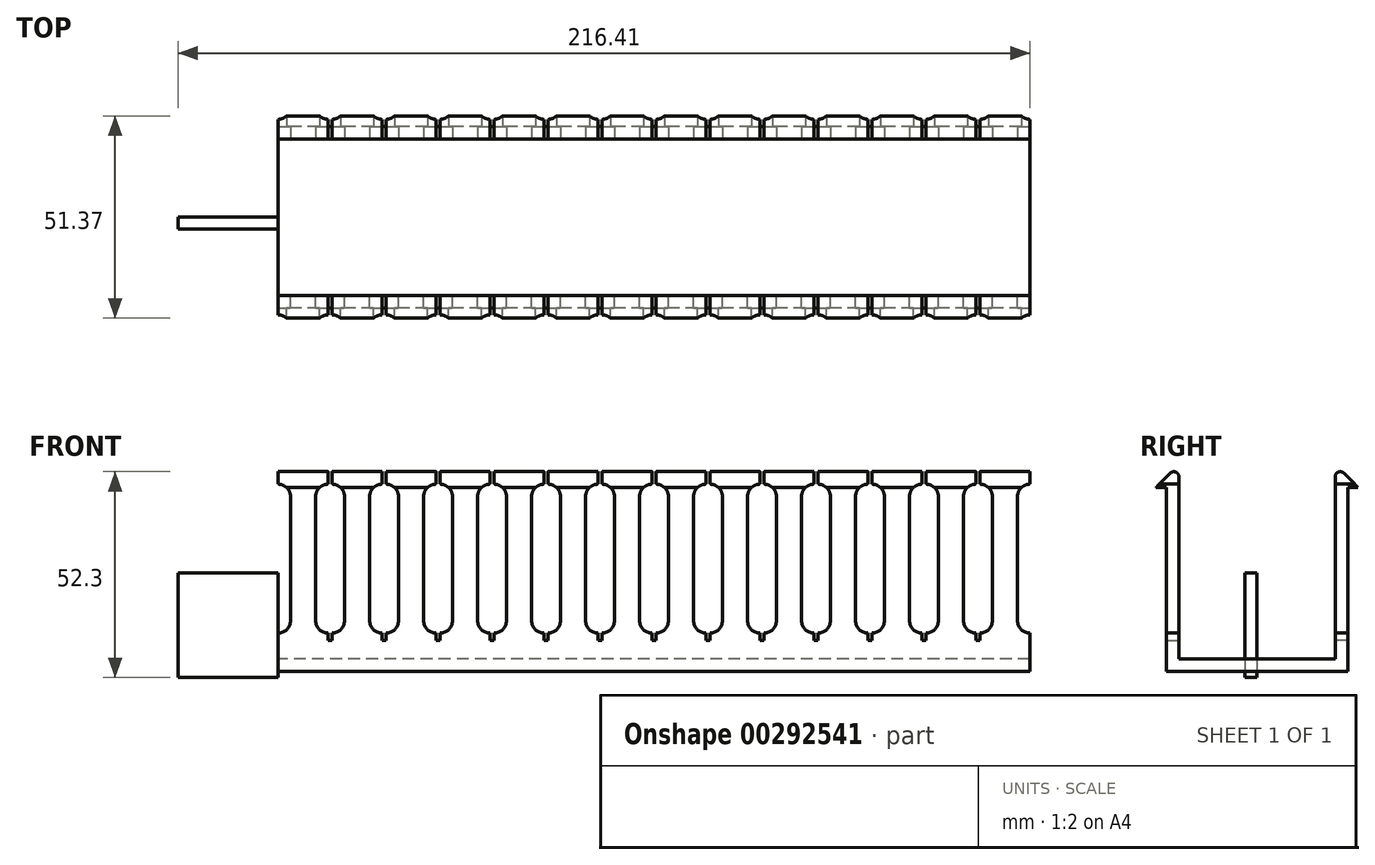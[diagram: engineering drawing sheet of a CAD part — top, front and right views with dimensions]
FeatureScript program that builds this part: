
annotation { "Feature Type Name" : "Feature", "Feature Type Description" : "" }
export const myFeature = defineFeature(function(context is Context, id is Id, definition is map)
    precondition{}
    {
        {
            var Q0;
            Q0=qCreatedBy(makeId("Front.planeOp"),FACE);
            var sketch = newSketch(context, id + "F0", { "sketchPlane" : qUnion([Q0])});
            skLineSegment(sketch, "E0", {"start": v(0, 47.62) * mm, "end": v(0, 50.8) * mm});
            skLineSegment(sketch, "E1", {"start": v(0, 50.8) * mm, "end": v(12.7, 50.8) * mm});
            skLineSegment(sketch, "E2", {"start": v(12.7, 50.8) * mm, "end": v(12.7, 47.62) * mm});
            skArc(sketch, "E3", {"start": v(3.18, 44.45) * mm, "mid": v(2.25, 46.7) * mm, "end": v(0, 47.62) * mm});
            skArc(sketch, "E4", {"start": v(12.7, 47.62) * mm, "mid": v(10.45, 46.7) * mm, "end": v(9.53, 44.45) * mm});
            skLineSegment(sketch, "E5", {"start": v(3.18, 44.45) * mm, "end": v(3.18, 12.95) * mm});
            skLineSegment(sketch, "E6", {"start": v(9.53, 44.45) * mm, "end": v(9.53, 12.95) * mm});
            skArc(sketch, "E7", {"start": v(3.18, 12.95) * mm, "mid": v(2.25, 10.7) * mm, "end": v(0, 9.78) * mm});
            skArc(sketch, "E8", {"start": v(9.53, 12.95) * mm, "mid": v(10.45, 10.7) * mm, "end": v(12.7, 9.78) * mm});
            skLineSegment(sketch, "E9", {"start": v(0, 9.78) * mm, "end": v(0, 0) * mm});
            skLineSegment(sketch, "E10", {"start": v(0, 0) * mm, "end": v(191, 0) * mm});
            skLineSegment(sketch, "E11", {"start": v(13.2, 7.13) * mm, "end": v(13.2, 52.31) * mm, "construction": true});
            skLineSegment(sketch, "E12.MirrorCS", {"start": v(13.72, 50.8) * mm, "end": v(13.72, 47.62) * mm});
            skArc(sketch, "E13.MirrorCS", {"start": v(13.72, 47.62) * mm, "mid": v(15.96, 46.7) * mm, "end": v(16.9, 44.45) * mm});
            skLineSegment(sketch, "E14.MirrorCS", {"start": v(16.9, 44.45) * mm, "end": v(16.9, 12.95) * mm});
            skArc(sketch, "E15.MirrorCS", {"start": v(16.9, 12.95) * mm, "mid": v(15.96, 10.7) * mm, "end": v(13.72, 9.78) * mm});
            skLineSegment(sketch, "E16.MirrorCS", {"start": v(26.42, 50.8) * mm, "end": v(13.72, 50.8) * mm});
            skLineSegment(sketch, "E17.MirrorCS", {"start": v(26.42, 47.62) * mm, "end": v(26.42, 50.8) * mm});
            skArc(sketch, "E18.MirrorCS", {"start": v(23.24, 44.45) * mm, "mid": v(24.17, 46.7) * mm, "end": v(26.42, 47.62) * mm});
            skLineSegment(sketch, "E19.MirrorCS", {"start": v(23.24, 44.45) * mm, "end": v(23.24, 12.95) * mm});
            skArc(sketch, "E20.MirrorCS", {"start": v(23.24, 12.95) * mm, "mid": v(24.17, 10.7) * mm, "end": v(26.42, 9.78) * mm});
            skLineSegment(sketch, "E21", {"start": v(26.92, 7.21) * mm, "end": v(26.92, 55.4) * mm, "construction": true});
            skLineSegment(sketch, "E22.MirrorCS", {"start": v(27.43, 47.62) * mm, "end": v(27.43, 50.8) * mm});
            skArc(sketch, "E23.MirrorCS", {"start": v(30.6, 44.45) * mm, "mid": v(29.68, 46.7) * mm, "end": v(27.43, 47.62) * mm});
            skLineSegment(sketch, "E24.MirrorCS", {"start": v(30.6, 44.45) * mm, "end": v(30.6, 12.95) * mm});
            skArc(sketch, "E25.MirrorCS", {"start": v(30.6, 12.95) * mm, "mid": v(29.68, 10.7) * mm, "end": v(27.43, 9.78) * mm});
            skLineSegment(sketch, "E26.MirrorCS", {"start": v(27.43, 50.8) * mm, "end": v(40.13, 50.8) * mm});
            skLineSegment(sketch, "E27.MirrorCS", {"start": v(40.13, 50.8) * mm, "end": v(40.13, 47.62) * mm});
            skArc(sketch, "E28.MirrorCS", {"start": v(40.13, 47.62) * mm, "mid": v(37.89, 46.7) * mm, "end": v(36.96, 44.45) * mm});
            skLineSegment(sketch, "E29.MirrorCS", {"start": v(36.96, 44.45) * mm, "end": v(36.96, 12.95) * mm});
            skArc(sketch, "E30.MirrorCS", {"start": v(36.96, 12.95) * mm, "mid": v(37.89, 10.7) * mm, "end": v(40.13, 9.78) * mm});
            skLineSegment(sketch, "E31", {"start": v(40.64, 6.35) * mm, "end": v(40.64, 55.95) * mm, "construction": true});
            skLineSegment(sketch, "E32.MirrorCS", {"start": v(41.15, 50.8) * mm, "end": v(41.15, 47.62) * mm});
            skLineSegment(sketch, "E33.MirrorCS", {"start": v(53.85, 50.8) * mm, "end": v(41.15, 50.8) * mm});
            skArc(sketch, "E34.MirrorCS", {"start": v(41.15, 47.62) * mm, "mid": v(43.4, 46.7) * mm, "end": v(44.32, 44.45) * mm});
            skArc(sketch, "E35.MirrorCS", {"start": v(50.67, 44.45) * mm, "mid": v(51.6, 46.7) * mm, "end": v(53.85, 47.62) * mm});
            skLineSegment(sketch, "E36.MirrorCS", {"start": v(50.67, 44.45) * mm, "end": v(50.67, 12.95) * mm});
            skLineSegment(sketch, "E37.MirrorCS", {"start": v(44.32, 44.45) * mm, "end": v(44.32, 12.95) * mm});
            skArc(sketch, "E38.MirrorCS", {"start": v(50.67, 12.95) * mm, "mid": v(51.6, 10.7) * mm, "end": v(53.85, 9.78) * mm});
            skArc(sketch, "E39.MirrorCS", {"start": v(44.32, 12.95) * mm, "mid": v(43.4, 10.7) * mm, "end": v(41.15, 9.78) * mm});
            skLineSegment(sketch, "E40.MirrorCS", {"start": v(53.85, 47.62) * mm, "end": v(53.85, 50.8) * mm});
            skLineSegment(sketch, "E41.MirrorCS", {"start": v(54.86, 47.62) * mm, "end": v(54.86, 50.8) * mm});
            skLineSegment(sketch, "E42.MirrorCS", {"start": v(54.86, 50.8) * mm, "end": v(67.56, 50.8) * mm});
            skLineSegment(sketch, "E43.MirrorCS", {"start": v(58.04, 44.45) * mm, "end": v(58.04, 12.95) * mm});
            skArc(sketch, "E44.MirrorCS", {"start": v(58.04, 44.45) * mm, "mid": v(57.1, 46.7) * mm, "end": v(54.86, 47.62) * mm});
            skArc(sketch, "E45.MirrorCS", {"start": v(58.04, 12.95) * mm, "mid": v(57.1, 10.7) * mm, "end": v(54.86, 9.78) * mm});
            skLineSegment(sketch, "E46.MirrorCS", {"start": v(67.56, 50.8) * mm, "end": v(67.56, 47.62) * mm});
            skArc(sketch, "E47.MirrorCS", {"start": v(67.56, 47.62) * mm, "mid": v(65.32, 46.7) * mm, "end": v(64.39, 44.45) * mm});
            skLineSegment(sketch, "E48.MirrorCS", {"start": v(64.39, 44.45) * mm, "end": v(64.39, 12.95) * mm});
            skArc(sketch, "E49.MirrorCS", {"start": v(64.39, 12.95) * mm, "mid": v(65.32, 10.7) * mm, "end": v(67.56, 9.78) * mm});
            skArc(sketch, "E50.MirrorCS", {"start": v(68.58, 47.62) * mm, "mid": v(70.83, 46.7) * mm, "end": v(71.76, 44.45) * mm});
            skLineSegment(sketch, "E51.MirrorCS", {"start": v(68.58, 50.8) * mm, "end": v(68.58, 47.62) * mm});
            skLineSegment(sketch, "E52.MirrorCS", {"start": v(81.28, 50.8) * mm, "end": v(68.58, 50.8) * mm});
            skLineSegment(sketch, "E53.MirrorCS", {"start": v(81.28, 47.62) * mm, "end": v(81.28, 50.8) * mm});
            skArc(sketch, "E54.MirrorCS", {"start": v(78.1, 44.45) * mm, "mid": v(79.03, 46.7) * mm, "end": v(81.28, 47.62) * mm});
            skLineSegment(sketch, "E55.MirrorCS", {"start": v(78.1, 44.45) * mm, "end": v(78.1, 12.95) * mm});
            skLineSegment(sketch, "E56.MirrorCS", {"start": v(71.76, 44.45) * mm, "end": v(71.76, 12.95) * mm});
            skArc(sketch, "E57.MirrorCS", {"start": v(71.76, 12.95) * mm, "mid": v(70.83, 10.7) * mm, "end": v(68.58, 9.78) * mm});
            skArc(sketch, "E58.MirrorCS", {"start": v(78.1, 12.95) * mm, "mid": v(79.03, 10.7) * mm, "end": v(81.28, 9.78) * mm});
            skLineSegment(sketch, "E59", {"start": v(81.79, 5.79) * mm, "end": v(81.79, 59.1) * mm, "construction": true});
            skLineSegment(sketch, "E60.MirrorCS", {"start": v(109.73, 47.62) * mm, "end": v(109.73, 50.8) * mm});
            skLineSegment(sketch, "E61.MirrorCS", {"start": v(108.71, 47.62) * mm, "end": v(108.71, 50.8) * mm});
            skArc(sketch, "E62.MirrorCS", {"start": v(112.9, 44.45) * mm, "mid": v(111.97, 46.7) * mm, "end": v(109.73, 47.62) * mm});
            skLineSegment(sketch, "E63.MirrorCS", {"start": v(122.43, 50.8) * mm, "end": v(122.43, 47.62) * mm});
            skLineSegment(sketch, "E64.MirrorCS", {"start": v(123.44, 50.8) * mm, "end": v(123.44, 47.62) * mm});
            skArc(sketch, "E65.MirrorCS", {"start": v(96.01, 47.62) * mm, "mid": v(98.26, 46.7) * mm, "end": v(99.19, 44.45) * mm});
            skArc(sketch, "E66.MirrorCS", {"start": v(122.43, 47.62) * mm, "mid": v(120.18, 46.7) * mm, "end": v(119.25, 44.45) * mm});
            skLineSegment(sketch, "E67.MirrorCS", {"start": v(96.01, 50.8) * mm, "end": v(96.01, 47.62) * mm});
            skLineSegment(sketch, "E68.MirrorCS", {"start": v(95, 50.8) * mm, "end": v(95, 47.62) * mm});
            skLineSegment(sketch, "E69.MirrorCS", {"start": v(136.14, 47.62) * mm, "end": v(136.14, 50.8) * mm});
            skArc(sketch, "E70.MirrorCS", {"start": v(132.97, 12.95) * mm, "mid": v(133.9, 10.7) * mm, "end": v(136.14, 9.78) * mm});
            skArc(sketch, "E71.MirrorCS", {"start": v(149.86, 47.62) * mm, "mid": v(147.61, 46.7) * mm, "end": v(146.69, 44.45) * mm});
            skLineSegment(sketch, "E72.MirrorCS", {"start": v(150.88, 50.8) * mm, "end": v(150.88, 47.62) * mm});
            skLineSegment(sketch, "E73.MirrorCS", {"start": v(137.16, 47.62) * mm, "end": v(137.16, 50.8) * mm});
            skArc(sketch, "E74.MirrorCS", {"start": v(99.19, 12.95) * mm, "mid": v(98.26, 10.7) * mm, "end": v(96.01, 9.78) * mm});
            skLineSegment(sketch, "E75.MirrorCS", {"start": v(149.86, 50.8) * mm, "end": v(149.86, 47.62) * mm});
            skArc(sketch, "E76.MirrorCS", {"start": v(140.34, 12.95) * mm, "mid": v(139.4, 10.7) * mm, "end": v(137.16, 9.78) * mm});
            skArc(sketch, "E77.MirrorCS", {"start": v(140.34, 44.45) * mm, "mid": v(139.4, 46.7) * mm, "end": v(137.16, 47.62) * mm});
            skArc(sketch, "E78.MirrorCS", {"start": v(112.9, 12.95) * mm, "mid": v(111.97, 10.7) * mm, "end": v(109.73, 9.78) * mm});
            skArc(sketch, "E79.MirrorCS", {"start": v(95, 47.62) * mm, "mid": v(92.75, 46.7) * mm, "end": v(91.82, 44.45) * mm});
            skArc(sketch, "E80.MirrorCS", {"start": v(91.82, 12.95) * mm, "mid": v(92.75, 10.7) * mm, "end": v(95, 9.78) * mm});
            skArc(sketch, "E81.MirrorCS", {"start": v(105.54, 44.45) * mm, "mid": v(106.47, 46.7) * mm, "end": v(108.71, 47.62) * mm});
            skArc(sketch, "E82.MirrorCS", {"start": v(146.69, 12.95) * mm, "mid": v(147.61, 10.7) * mm, "end": v(149.86, 9.78) * mm});
            skLineSegment(sketch, "E83.MirrorCS", {"start": v(163.58, 47.62) * mm, "end": v(163.58, 50.8) * mm});
            skArc(sketch, "E84.MirrorCS", {"start": v(105.54, 12.95) * mm, "mid": v(106.47, 10.7) * mm, "end": v(108.71, 9.78) * mm});
            skArc(sketch, "E85.MirrorCS", {"start": v(160.4, 44.45) * mm, "mid": v(161.33, 46.7) * mm, "end": v(163.58, 47.62) * mm});
            skArc(sketch, "E86.MirrorCS", {"start": v(123.44, 47.62) * mm, "mid": v(125.69, 46.7) * mm, "end": v(126.62, 44.45) * mm});
            skArc(sketch, "E87.MirrorCS", {"start": v(150.88, 47.62) * mm, "mid": v(153.12, 46.7) * mm, "end": v(154.05, 44.45) * mm});
            skArc(sketch, "E88.MirrorCS", {"start": v(154.05, 12.95) * mm, "mid": v(153.12, 10.7) * mm, "end": v(150.88, 9.78) * mm});
            skArc(sketch, "E89.MirrorCS", {"start": v(160.4, 12.95) * mm, "mid": v(161.33, 10.7) * mm, "end": v(163.58, 9.78) * mm});
            skLineSegment(sketch, "E90.MirrorCS", {"start": v(85.47, 44.45) * mm, "end": v(85.47, 12.95) * mm});
            skArc(sketch, "E91.MirrorCS", {"start": v(126.62, 12.95) * mm, "mid": v(125.69, 10.7) * mm, "end": v(123.44, 9.78) * mm});
            skArc(sketch, "E92.MirrorCS", {"start": v(119.25, 12.95) * mm, "mid": v(120.18, 10.7) * mm, "end": v(122.43, 9.78) * mm});
            skArc(sketch, "E93.MirrorCS", {"start": v(132.97, 44.45) * mm, "mid": v(133.9, 46.7) * mm, "end": v(136.14, 47.62) * mm});
            skLineSegment(sketch, "E94.MirrorCS", {"start": v(99.19, 44.45) * mm, "end": v(99.19, 12.95) * mm});
            skLineSegment(sketch, "E95.MirrorCS", {"start": v(122.94, 6.35) * mm, "end": v(122.94, 55.95) * mm, "construction": true});
            skLineSegment(sketch, "E96.MirrorCS", {"start": v(136.14, 50.8) * mm, "end": v(123.44, 50.8) * mm});
            skLineSegment(sketch, "E97.MirrorCS", {"start": v(140.34, 44.45) * mm, "end": v(140.34, 12.95) * mm});
            skLineSegment(sketch, "E98.MirrorCS", {"start": v(146.69, 44.45) * mm, "end": v(146.69, 12.95) * mm});
            skLineSegment(sketch, "E99.MirrorCS", {"start": v(163.58, 50.8) * mm, "end": v(150.88, 50.8) * mm});
            skLineSegment(sketch, "E100.MirrorCS", {"start": v(109.73, 50.8) * mm, "end": v(122.43, 50.8) * mm});
            skLineSegment(sketch, "E101.MirrorCS", {"start": v(137.16, 50.8) * mm, "end": v(149.86, 50.8) * mm});
            skLineSegment(sketch, "E102.MirrorCS", {"start": v(126.62, 44.45) * mm, "end": v(126.62, 12.95) * mm});
            skLineSegment(sketch, "E103.MirrorCS", {"start": v(154.05, 44.45) * mm, "end": v(154.05, 12.95) * mm});
            skLineSegment(sketch, "E104.MirrorCS", {"start": v(119.25, 44.45) * mm, "end": v(119.25, 12.95) * mm});
            skLineSegment(sketch, "E105.MirrorCS", {"start": v(112.9, 44.45) * mm, "end": v(112.9, 12.95) * mm});
            skLineSegment(sketch, "E106.MirrorCS", {"start": v(105.54, 44.45) * mm, "end": v(105.54, 12.95) * mm});
            skLineSegment(sketch, "E107.MirrorCS", {"start": v(91.82, 44.45) * mm, "end": v(91.82, 12.95) * mm});
            skLineSegment(sketch, "E108.MirrorCS", {"start": v(150.37, 7.13) * mm, "end": v(150.37, 52.31) * mm, "construction": true});
            skLineSegment(sketch, "E109.MirrorCS", {"start": v(160.4, 44.45) * mm, "end": v(160.4, 12.95) * mm});
            skLineSegment(sketch, "E110.MirrorCS", {"start": v(108.71, 50.8) * mm, "end": v(96.01, 50.8) * mm});
            skLineSegment(sketch, "E111.MirrorCS", {"start": v(136.65, 7.21) * mm, "end": v(136.65, 55.4) * mm, "construction": true});
            skLineSegment(sketch, "E112.MirrorCS", {"start": v(132.97, 44.45) * mm, "end": v(132.97, 12.95) * mm});
            skLineSegment(sketch, "E113.MirrorCS", {"start": v(82.3, 50.8) * mm, "end": v(95, 50.8) * mm});
            skArc(sketch, "E114.MirrorCS", {"start": v(85.47, 44.45) * mm, "mid": v(84.54, 46.7) * mm, "end": v(82.3, 47.62) * mm});
            skLineSegment(sketch, "E115", {"start": v(164.08, 5.68) * mm, "end": v(164.08, 52.1) * mm, "construction": true});
            skLineSegment(sketch, "E116.MirrorCS", {"start": v(164.6, 50.8) * mm, "end": v(177.3, 50.8) * mm});
            skLineSegment(sketch, "E117.MirrorCS", {"start": v(164.6, 47.62) * mm, "end": v(164.6, 50.8) * mm});
            skArc(sketch, "E118.MirrorCS", {"start": v(167.77, 44.45) * mm, "mid": v(166.84, 46.7) * mm, "end": v(164.6, 47.62) * mm});
            skLineSegment(sketch, "E119.MirrorCS", {"start": v(167.77, 44.45) * mm, "end": v(167.77, 12.95) * mm});
            skArc(sketch, "E120.MirrorCS", {"start": v(167.77, 12.95) * mm, "mid": v(166.84, 10.7) * mm, "end": v(164.6, 9.78) * mm});
            skLineSegment(sketch, "E121.MirrorCS", {"start": v(174.12, 44.45) * mm, "end": v(174.12, 12.95) * mm});
            skArc(sketch, "E122.MirrorCS", {"start": v(177.3, 47.63) * mm, "mid": v(175.05, 46.7) * mm, "end": v(174.12, 44.45) * mm});
            skLineSegment(sketch, "E123.MirrorCS", {"start": v(177.8, 7.13) * mm, "end": v(177.8, 52.31) * mm, "construction": true});
            skArc(sketch, "E124.MirrorCS", {"start": v(174.12, 12.95) * mm, "mid": v(175.05, 10.7) * mm, "end": v(177.3, 9.78) * mm});
            skArc(sketch, "E125.MirrorCS", {"start": v(181.48, 12.95) * mm, "mid": v(180.55, 10.7) * mm, "end": v(178.3, 9.78) * mm});
            skLineSegment(sketch, "E126.MirrorCS", {"start": v(181.48, 44.45) * mm, "end": v(181.48, 12.95) * mm});
            skArc(sketch, "E127.MirrorCS", {"start": v(178.3, 47.63) * mm, "mid": v(180.55, 46.7) * mm, "end": v(181.48, 44.45) * mm});
            skLineSegment(sketch, "E128.MirrorCS", {"start": v(178.3, 50.8) * mm, "end": v(178.3, 47.63) * mm});
            skLineSegment(sketch, "E129.MirrorCS", {"start": v(191, 50.8) * mm, "end": v(178.3, 50.8) * mm});
            skLineSegment(sketch, "E130.MirrorCS", {"start": v(191, 47.63) * mm, "end": v(191, 50.8) * mm});
            skArc(sketch, "E131.MirrorCS", {"start": v(187.83, 44.45) * mm, "mid": v(188.76, 46.7) * mm, "end": v(191, 47.63) * mm});
            skLineSegment(sketch, "E132.MirrorCS", {"start": v(187.83, 44.45) * mm, "end": v(187.83, 12.95) * mm});
            skArc(sketch, "E133.MirrorCS", {"start": v(187.83, 12.95) * mm, "mid": v(188.76, 10.7) * mm, "end": v(191, 9.78) * mm});
            skLineSegment(sketch, "E134", {"start": v(191, 9.78) * mm, "end": v(191, 0) * mm});
            skArc(sketch, "E135.MirrorCS", {"start": v(85.47, 12.95) * mm, "mid": v(84.54, 10.7) * mm, "end": v(82.3, 9.78) * mm});
            skLineSegment(sketch, "E136", {"start": v(12.7, 9.78) * mm, "end": v(12.7, 7.87) * mm});
            skLineSegment(sketch, "E137", {"start": v(12.7, 7.87) * mm, "end": v(13.72, 7.87) * mm});
            skLineSegment(sketch, "E138", {"start": v(13.72, 7.87) * mm, "end": v(13.72, 9.78) * mm});
            skLineSegment(sketch, "E139", {"start": v(26.42, 9.78) * mm, "end": v(26.42, 7.87) * mm});
            skLineSegment(sketch, "E140", {"start": v(26.42, 7.87) * mm, "end": v(27.43, 7.87) * mm});
            skLineSegment(sketch, "E141", {"start": v(27.43, 7.87) * mm, "end": v(27.43, 9.78) * mm});
            skLineSegment(sketch, "E142", {"start": v(40.13, 9.78) * mm, "end": v(40.13, 7.87) * mm});
            skLineSegment(sketch, "E143", {"start": v(40.13, 7.87) * mm, "end": v(41.15, 7.87) * mm});
            skLineSegment(sketch, "E144", {"start": v(41.15, 7.87) * mm, "end": v(41.15, 9.78) * mm});
            skLineSegment(sketch, "E145", {"start": v(53.85, 9.78) * mm, "end": v(53.85, 7.87) * mm});
            skLineSegment(sketch, "E146", {"start": v(54.86, 9.78) * mm, "end": v(54.86, 7.87) * mm});
            skLineSegment(sketch, "E147", {"start": v(54.86, 7.87) * mm, "end": v(53.85, 7.87) * mm});
            skLineSegment(sketch, "E148", {"start": v(67.56, 9.78) * mm, "end": v(67.56, 7.87) * mm});
            skLineSegment(sketch, "E149", {"start": v(68.58, 9.78) * mm, "end": v(68.58, 7.87) * mm});
            skLineSegment(sketch, "E150", {"start": v(68.58, 7.87) * mm, "end": v(67.56, 7.87) * mm});
            skLineSegment(sketch, "E151", {"start": v(81.28, 9.78) * mm, "end": v(81.28, 7.87) * mm});
            skLineSegment(sketch, "E152", {"start": v(82.3, 9.78) * mm, "end": v(82.3, 7.87) * mm});
            skLineSegment(sketch, "E153", {"start": v(82.3, 7.87) * mm, "end": v(81.28, 7.87) * mm});
            skLineSegment(sketch, "E154", {"start": v(95, 9.78) * mm, "end": v(95, 7.87) * mm});
            skLineSegment(sketch, "E155", {"start": v(95, 7.87) * mm, "end": v(96.01, 7.87) * mm});
            skLineSegment(sketch, "E156", {"start": v(96.01, 7.87) * mm, "end": v(96.01, 9.78) * mm});
            skLineSegment(sketch, "E157", {"start": v(108.71, 9.78) * mm, "end": v(108.71, 7.87) * mm});
            skLineSegment(sketch, "E158", {"start": v(108.71, 7.87) * mm, "end": v(109.73, 7.87) * mm});
            skLineSegment(sketch, "E159", {"start": v(109.73, 7.87) * mm, "end": v(109.73, 9.78) * mm});
            skLineSegment(sketch, "E160", {"start": v(122.43, 9.78) * mm, "end": v(122.43, 7.87) * mm});
            skLineSegment(sketch, "E161", {"start": v(122.43, 7.87) * mm, "end": v(123.44, 7.87) * mm});
            skLineSegment(sketch, "E162", {"start": v(123.44, 7.87) * mm, "end": v(123.44, 9.78) * mm});
            skLineSegment(sketch, "E163", {"start": v(136.14, 9.78) * mm, "end": v(136.14, 7.87) * mm});
            skLineSegment(sketch, "E164", {"start": v(136.14, 7.87) * mm, "end": v(137.16, 7.87) * mm});
            skLineSegment(sketch, "E165", {"start": v(137.16, 7.87) * mm, "end": v(137.16, 9.78) * mm});
            skLineSegment(sketch, "E166", {"start": v(149.86, 9.78) * mm, "end": v(149.86, 7.87) * mm});
            skLineSegment(sketch, "E167", {"start": v(150.88, 9.78) * mm, "end": v(150.88, 7.87) * mm});
            skLineSegment(sketch, "E168", {"start": v(150.88, 7.87) * mm, "end": v(149.86, 7.87) * mm});
            skLineSegment(sketch, "E169", {"start": v(163.58, 9.78) * mm, "end": v(163.58, 7.87) * mm});
            skLineSegment(sketch, "E170", {"start": v(163.58, 7.87) * mm, "end": v(164.6, 7.87) * mm});
            skLineSegment(sketch, "E171", {"start": v(164.6, 7.87) * mm, "end": v(164.6, 9.78) * mm});
            skLineSegment(sketch, "E172", {"start": v(177.3, 9.78) * mm, "end": v(177.3, 7.87) * mm});
            skLineSegment(sketch, "E173", {"start": v(178.3, 9.78) * mm, "end": v(178.3, 7.87) * mm});
            skLineSegment(sketch, "E174", {"start": v(178.3, 7.87) * mm, "end": v(177.3, 7.87) * mm});
            skLineSegment(sketch, "E175", {"start": v(177.3, 50.8) * mm, "end": v(177.3, 47.63) * mm});
            skLineSegment(sketch, "E176", {"start": v(82.3, 50.8) * mm, "end": v(82.3, 47.62) * mm});
            skSolve(sketch);
        }
        {
            var Q0;
            Q0 = qSketchRegion(id + "F0", true);
            extrude(context, id + "F1", {"entities" : qUnion([Q0]), "depth" : 3.17 * mm});
        }
        {
            var Q0;
            Q0=makeQuery(id+"F1.opExtrude","SWEPT_FACE",FACE,{"disambiguationData":[OSD([sQuery(id+"F0.wireOp",EDGE,"E0")])]});
            var sketch = newSketch(context, id + "F2", { "sketchPlane" : qUnion([Q0])});
            skLineSegment(sketch, "E177.0.0", {"start": v(0, 50.8) * mm, "end": v(0, 49.53) * mm});
            skLineSegment(sketch, "E177.0.3", {"start": v(1.27, 50.8) * mm, "end": v(0, 50.8) * mm});
            skArc(sketch, "E178", {"start": v(1.27, 50.8) * mm, "mid": v(0.37, 50.43) * mm, "end": v(0, 49.53) * mm});
            skPoint(sketch, "E179.orphan", {"position": v(0, 47.62) * mm});
            skPoint(sketch, "E180.orphan", {"position": v(3.18, 47.62) * mm});
            skPoint(sketch, "E177.0.2.end.orphan", {"position": v(3.18, 50.8) * mm});
            skPoint(sketch, "E181.end.orphan", {"position": v(3.18, 46.78) * mm});
            skArc(sketch, "E182", {"start": v(2.17, 50.43) * mm, "mid": v(1.76, 50.7) * mm, "end": v(1.27, 50.8) * mm});
            skLineSegment(sketch, "E183", {"start": v(2.17, 50.43) * mm, "end": v(5.74, 46.86) * mm});
            skLineSegment(sketch, "E184", {"start": v(3.18, 50.8) * mm, "end": v(3.18, 49.42) * mm});
            skLineSegment(sketch, "E185", {"start": v(3.18, 50.8) * mm, "end": v(1.27, 50.8) * mm});
            skSolve(sketch);
        }
        {
            var Q0;
            Q0 = qSketchRegion(id + "F2", true);
            extrude(context, id + "F3", {"entities" : qUnion([Q0]), "operationType" : NewBodyOperationType.REMOVE, "endBound" : BoundingType.THROUGH_ALL, "oppositeDirection" : true, "depth" : 25.4 * mm});
        }
        {
            var Q0;
            Q0 = qSketchRegion(id + "F2", true);
            extrude(context, id + "F4", {"entities" : qUnion([Q0]), "operationType" : NewBodyOperationType.REMOVE, "endBound" : BoundingType.THROUGH_ALL, "oppositeDirection" : true, "depth" : 25.4 * mm});
        }
        {
            var Q0;
            Q0=makeQuery(id+"F1.opExtrude","SWEPT_FACE",FACE,{"disambiguationData":[OSD([sQuery(id+"F0.wireOp",EDGE,"E0")])]});
            var sketch = newSketch(context, id + "F5", { "sketchPlane" : qUnion([Q0])});
            skLineSegment(sketch, "E186", {"start": v(3.17, 49.42) * mm, "end": v(5.82, 46.78) * mm});
            skLineSegment(sketch, "E187", {"start": v(5.82, 46.78) * mm, "end": v(3.18, 46.78) * mm});
            skLineSegment(sketch, "E188", {"start": v(3.17, 46.78) * mm, "end": v(3.18, 49.42) * mm});
            skSolve(sketch);
        }
        {
            var Q0;
            Q0 = qSketchRegion(id + "F5", true);
            extrude(context, id + "F6", {"entities" : qUnion([Q0]), "operationType" : NewBodyOperationType.ADD, "oppositeDirection" : true, "depth" : 191 * mm});
        }
        {
            var Q0;
            Q0=makeQuery(id+"F1.opExtrude","CAP_FACE",FACE,{"disambiguationData":[OSD([sQuery(id+"F0.wireOp",EDGE,"E0"),sQuery(id+"F0.wireOp",EDGE,"E1"),sQuery(id+"F0.wireOp",EDGE,"E2"),sQuery(id+"F0.wireOp",EDGE,"E3"),sQuery(id+"F0.wireOp",EDGE,"E4"),sQuery(id+"F0.wireOp",EDGE,"E5"),sQuery(id+"F0.wireOp",EDGE,"E6"),sQuery(id+"F0.wireOp",EDGE,"E7"),sQuery(id+"F0.wireOp",EDGE,"E8"),sQuery(id+"F0.wireOp",EDGE,"E9"),sQuery(id+"F0.wireOp",EDGE,"E10"),sQuery(id+"F0.wireOp",EDGE,"E12.MirrorCS"),sQuery(id+"F0.wireOp",EDGE,"E13.MirrorCS"),sQuery(id+"F0.wireOp",EDGE,"E14.MirrorCS"),sQuery(id+"F0.wireOp",EDGE,"E15.MirrorCS"),sQuery(id+"F0.wireOp",EDGE,"E16.MirrorCS"),sQuery(id+"F0.wireOp",EDGE,"E17.MirrorCS"),sQuery(id+"F0.wireOp",EDGE,"E18.MirrorCS"),sQuery(id+"F0.wireOp",EDGE,"E19.MirrorCS"),sQuery(id+"F0.wireOp",EDGE,"E20.MirrorCS"),sQuery(id+"F0.wireOp",EDGE,"E22.MirrorCS"),sQuery(id+"F0.wireOp",EDGE,"E23.MirrorCS"),sQuery(id+"F0.wireOp",EDGE,"E24.MirrorCS"),sQuery(id+"F0.wireOp",EDGE,"E25.MirrorCS"),sQuery(id+"F0.wireOp",EDGE,"E26.MirrorCS"),sQuery(id+"F0.wireOp",EDGE,"E27.MirrorCS"),sQuery(id+"F0.wireOp",EDGE,"E28.MirrorCS"),sQuery(id+"F0.wireOp",EDGE,"E29.MirrorCS"),sQuery(id+"F0.wireOp",EDGE,"E30.MirrorCS"),sQuery(id+"F0.wireOp",EDGE,"E32.MirrorCS"),sQuery(id+"F0.wireOp",EDGE,"E33.MirrorCS"),sQuery(id+"F0.wireOp",EDGE,"E35.MirrorCS"),sQuery(id+"F0.wireOp",EDGE,"E36.MirrorCS"),sQuery(id+"F0.wireOp",EDGE,"E37.MirrorCS"),sQuery(id+"F0.wireOp",EDGE,"E38.MirrorCS"),sQuery(id+"F0.wireOp",EDGE,"E39.MirrorCS"),sQuery(id+"F0.wireOp",EDGE,"E41.MirrorCS"),sQuery(id+"F0.wireOp",EDGE,"E34.MirrorCS"),sQuery(id+"F0.wireOp",EDGE,"E42.MirrorCS"),sQuery(id+"F0.wireOp",EDGE,"E40.MirrorCS"),sQuery(id+"F0.wireOp",EDGE,"E43.MirrorCS"),sQuery(id+"F0.wireOp",EDGE,"E44.MirrorCS"),sQuery(id+"F0.wireOp",EDGE,"E45.MirrorCS"),sQuery(id+"F0.wireOp",EDGE,"E46.MirrorCS"),sQuery(id+"F0.wireOp",EDGE,"E47.MirrorCS"),sQuery(id+"F0.wireOp",EDGE,"E49.MirrorCS"),sQuery(id+"F0.wireOp",EDGE,"E48.MirrorCS"),sQuery(id+"F0.wireOp",EDGE,"E50.MirrorCS"),sQuery(id+"F0.wireOp",EDGE,"E51.MirrorCS"),sQuery(id+"F0.wireOp",EDGE,"E52.MirrorCS"),sQuery(id+"F0.wireOp",EDGE,"E53.MirrorCS"),sQuery(id+"F0.wireOp",EDGE,"E54.MirrorCS"),sQuery(id+"F0.wireOp",EDGE,"E55.MirrorCS"),sQuery(id+"F0.wireOp",EDGE,"E56.MirrorCS"),sQuery(id+"F0.wireOp",EDGE,"E57.MirrorCS"),sQuery(id+"F0.wireOp",EDGE,"E58.MirrorCS"),sQuery(id+"F0.wireOp",EDGE,"E61.MirrorCS"),sQuery(id+"F0.wireOp",EDGE,"E62.MirrorCS"),sQuery(id+"F0.wireOp",EDGE,"E60.MirrorCS"),sQuery(id+"F0.wireOp",EDGE,"E63.MirrorCS"),sQuery(id+"F0.wireOp",EDGE,"E64.MirrorCS"),sQuery(id+"F0.wireOp",EDGE,"E65.MirrorCS"),sQuery(id+"F0.wireOp",EDGE,"E67.MirrorCS"),sQuery(id+"F0.wireOp",EDGE,"E68.MirrorCS"),sQuery(id+"F0.wireOp",EDGE,"E66.MirrorCS"),sQuery(id+"F0.wireOp",EDGE,"E69.MirrorCS"),sQuery(id+"F0.wireOp",EDGE,"E70.MirrorCS"),sQuery(id+"F0.wireOp",EDGE,"E71.MirrorCS"),sQuery(id+"F0.wireOp",EDGE,"E72.MirrorCS"),sQuery(id+"F0.wireOp",EDGE,"E73.MirrorCS"),sQuery(id+"F0.wireOp",EDGE,"E74.MirrorCS"),sQuery(id+"F0.wireOp",EDGE,"E75.MirrorCS"),sQuery(id+"F0.wireOp",EDGE,"E76.MirrorCS"),sQuery(id+"F0.wireOp",EDGE,"E77.MirrorCS"),sQuery(id+"F0.wireOp",EDGE,"E78.MirrorCS"),sQuery(id+"F0.wireOp",EDGE,"E79.MirrorCS"),sQuery(id+"F0.wireOp",EDGE,"E80.MirrorCS"),sQuery(id+"F0.wireOp",EDGE,"E81.MirrorCS"),sQuery(id+"F0.wireOp",EDGE,"E82.MirrorCS"),sQuery(id+"F0.wireOp",EDGE,"E83.MirrorCS"),sQuery(id+"F0.wireOp",EDGE,"E84.MirrorCS"),sQuery(id+"F0.wireOp",EDGE,"E85.MirrorCS"),sQuery(id+"F0.wireOp",EDGE,"E86.MirrorCS"),sQuery(id+"F0.wireOp",EDGE,"E87.MirrorCS"),sQuery(id+"F0.wireOp",EDGE,"E88.MirrorCS"),sQuery(id+"F0.wireOp",EDGE,"E89.MirrorCS"),sQuery(id+"F0.wireOp",EDGE,"E91.MirrorCS"),sQuery(id+"F0.wireOp",EDGE,"E92.MirrorCS"),sQuery(id+"F0.wireOp",EDGE,"E93.MirrorCS"),sQuery(id+"F0.wireOp",EDGE,"E96.MirrorCS"),sQuery(id+"F0.wireOp",EDGE,"E97.MirrorCS"),sQuery(id+"F0.wireOp",EDGE,"E98.MirrorCS"),sQuery(id+"F0.wireOp",EDGE,"E99.MirrorCS"),sQuery(id+"F0.wireOp",EDGE,"E100.MirrorCS"),sQuery(id+"F0.wireOp",EDGE,"E101.MirrorCS"),sQuery(id+"F0.wireOp",EDGE,"E102.MirrorCS"),sQuery(id+"F0.wireOp",EDGE,"E90.MirrorCS"),sQuery(id+"F0.wireOp",EDGE,"E103.MirrorCS"),sQuery(id+"F0.wireOp",EDGE,"E94.MirrorCS"),sQuery(id+"F0.wireOp",EDGE,"E104.MirrorCS"),sQuery(id+"F0.wireOp",EDGE,"E105.MirrorCS"),sQuery(id+"F0.wireOp",EDGE,"E106.MirrorCS"),sQuery(id+"F0.wireOp",EDGE,"E107.MirrorCS"),sQuery(id+"F0.wireOp",EDGE,"E109.MirrorCS"),sQuery(id+"F0.wireOp",EDGE,"E110.MirrorCS"),sQuery(id+"F0.wireOp",EDGE,"E112.MirrorCS"),sQuery(id+"F0.wireOp",EDGE,"E113.MirrorCS"),sQuery(id+"F0.wireOp",EDGE,"E114.MirrorCS"),sQuery(id+"F0.wireOp",EDGE,"E116.MirrorCS"),sQuery(id+"F0.wireOp",EDGE,"E117.MirrorCS"),sQuery(id+"F0.wireOp",EDGE,"E118.MirrorCS"),sQuery(id+"F0.wireOp",EDGE,"E119.MirrorCS"),sQuery(id+"F0.wireOp",EDGE,"E120.MirrorCS"),sQuery(id+"F0.wireOp",EDGE,"E121.MirrorCS"),sQuery(id+"F0.wireOp",EDGE,"E122.MirrorCS"),sQuery(id+"F0.wireOp",EDGE,"E124.MirrorCS"),sQuery(id+"F0.wireOp",EDGE,"E125.MirrorCS"),sQuery(id+"F0.wireOp",EDGE,"E126.MirrorCS"),sQuery(id+"F0.wireOp",EDGE,"E127.MirrorCS"),sQuery(id+"F0.wireOp",EDGE,"E128.MirrorCS"),sQuery(id+"F0.wireOp",EDGE,"E129.MirrorCS"),sQuery(id+"F0.wireOp",EDGE,"E130.MirrorCS"),sQuery(id+"F0.wireOp",EDGE,"E131.MirrorCS"),sQuery(id+"F0.wireOp",EDGE,"E132.MirrorCS"),sQuery(id+"F0.wireOp",EDGE,"E133.MirrorCS"),sQuery(id+"F0.wireOp",EDGE,"E134"),sQuery(id+"F0.wireOp",EDGE,"E135.MirrorCS"),sQuery(id+"F0.wireOp",EDGE,"E136"),sQuery(id+"F0.wireOp",EDGE,"E137"),sQuery(id+"F0.wireOp",EDGE,"E138"),sQuery(id+"F0.wireOp",EDGE,"E139"),sQuery(id+"F0.wireOp",EDGE,"E140"),sQuery(id+"F0.wireOp",EDGE,"E141"),sQuery(id+"F0.wireOp",EDGE,"E142"),sQuery(id+"F0.wireOp",EDGE,"E143"),sQuery(id+"F0.wireOp",EDGE,"E144"),sQuery(id+"F0.wireOp",EDGE,"E145"),sQuery(id+"F0.wireOp",EDGE,"E146"),sQuery(id+"F0.wireOp",EDGE,"E147"),sQuery(id+"F0.wireOp",EDGE,"E148"),sQuery(id+"F0.wireOp",EDGE,"E149"),sQuery(id+"F0.wireOp",EDGE,"E150"),sQuery(id+"F0.wireOp",EDGE,"E151"),sQuery(id+"F0.wireOp",EDGE,"E152"),sQuery(id+"F0.wireOp",EDGE,"E153"),sQuery(id+"F0.wireOp",EDGE,"E154"),sQuery(id+"F0.wireOp",EDGE,"E155"),sQuery(id+"F0.wireOp",EDGE,"E156"),sQuery(id+"F0.wireOp",EDGE,"E157"),sQuery(id+"F0.wireOp",EDGE,"E158"),sQuery(id+"F0.wireOp",EDGE,"E159"),sQuery(id+"F0.wireOp",EDGE,"E160"),sQuery(id+"F0.wireOp",EDGE,"E161"),sQuery(id+"F0.wireOp",EDGE,"E162"),sQuery(id+"F0.wireOp",EDGE,"E163"),sQuery(id+"F0.wireOp",EDGE,"E164"),sQuery(id+"F0.wireOp",EDGE,"E165"),sQuery(id+"F0.wireOp",EDGE,"E166"),sQuery(id+"F0.wireOp",EDGE,"E167"),sQuery(id+"F0.wireOp",EDGE,"E168"),sQuery(id+"F0.wireOp",EDGE,"E169"),sQuery(id+"F0.wireOp",EDGE,"E170"),sQuery(id+"F0.wireOp",EDGE,"E171"),sQuery(id+"F0.wireOp",EDGE,"E172"),sQuery(id+"F0.wireOp",EDGE,"E173"),sQuery(id+"F0.wireOp",EDGE,"E174"),sQuery(id+"F0.wireOp",EDGE,"E175"),sQuery(id+"F0.wireOp",EDGE,"E176")])],"isStart":false});
            var sketch = newSketch(context, id + "F7", { "sketchPlane" : qUnion([Q0])});
            skCircle(sketch, "E189", {"center": v(0, 44.45) * mm, "radius": 3.18 * mm});
            skCircle(sketch, "E190", {"center": v(12.7, 44.45) * mm, "radius": 3.17 * mm});
            skCircle(sketch, "E191", {"center": v(13.72, 44.45) * mm, "radius": 3.18 * mm});
            skCircle(sketch, "E192", {"center": v(26.42, 44.45) * mm, "radius": 3.17 * mm});
            skCircle(sketch, "E193", {"center": v(27.43, 44.45) * mm, "radius": 3.17 * mm});
            skCircle(sketch, "E194", {"center": v(40.13, 44.45) * mm, "radius": 3.18 * mm});
            skCircle(sketch, "E195", {"center": v(41.15, 44.45) * mm, "radius": 3.18 * mm});
            skCircle(sketch, "E196", {"center": v(53.85, 44.45) * mm, "radius": 3.17 * mm});
            skCircle(sketch, "E197", {"center": v(54.86, 44.45) * mm, "radius": 3.17 * mm});
            skCircle(sketch, "E198", {"center": v(67.56, 44.45) * mm, "radius": 3.17 * mm});
            skCircle(sketch, "E199", {"center": v(68.58, 44.45) * mm, "radius": 3.17 * mm});
            skCircle(sketch, "E200", {"center": v(81.28, 44.45) * mm, "radius": 3.17 * mm});
            skCircle(sketch, "E201", {"center": v(82.3, 44.45) * mm, "radius": 3.17 * mm});
            skCircle(sketch, "E202", {"center": v(95, 44.45) * mm, "radius": 3.17 * mm});
            skCircle(sketch, "E203", {"center": v(96.01, 44.45) * mm, "radius": 3.17 * mm});
            skCircle(sketch, "E204", {"center": v(108.71, 44.45) * mm, "radius": 3.17 * mm});
            skCircle(sketch, "E205", {"center": v(109.73, 44.45) * mm, "radius": 3.17 * mm});
            skCircle(sketch, "E206", {"center": v(122.43, 44.45) * mm, "radius": 3.17 * mm});
            skCircle(sketch, "E207", {"center": v(123.44, 44.45) * mm, "radius": 3.18 * mm});
            skCircle(sketch, "E208", {"center": v(136.14, 44.45) * mm, "radius": 3.18 * mm});
            skCircle(sketch, "E209", {"center": v(137.16, 44.45) * mm, "radius": 3.18 * mm});
            skCircle(sketch, "E210", {"center": v(149.86, 44.45) * mm, "radius": 3.18 * mm});
            skCircle(sketch, "E211", {"center": v(150.88, 44.45) * mm, "radius": 3.18 * mm});
            skCircle(sketch, "E212", {"center": v(163.58, 44.45) * mm, "radius": 3.18 * mm});
            skCircle(sketch, "E213", {"center": v(164.6, 44.45) * mm, "radius": 3.18 * mm});
            skCircle(sketch, "E214", {"center": v(177.3, 44.45) * mm, "radius": 3.17 * mm});
            skCircle(sketch, "E215", {"center": v(178.3, 44.45) * mm, "radius": 3.17 * mm});
            skCircle(sketch, "E216", {"center": v(191, 44.45) * mm, "radius": 3.18 * mm});
            skLineSegment(sketch, "E217.right", {"start": v(13.74, 49.43) * mm, "end": v(13.74, 46.28) * mm});
            skSolve(sketch);
        }
        {
            var Q0;
            Q0 = qSketchRegion(id + "F7", true);
            extrude(context, id + "F8", {"entities" : qUnion([Q0]), "operationType" : NewBodyOperationType.REMOVE, "endBound" : BoundingType.THROUGH_ALL, "depth" : 25.4 * mm});
        }
        {
            var Q0;
            {var subQ8=sQuery(id+"F0.wireOp",EDGE,"E122.MirrorCS");Q0=makeQuery(id+"F6.boolean.opBoolean","SPLIT",FACE,{"disambiguationData":[TD([makeQuery(id+"F1.opExtrude","SWEPT_FACE",FACE,{"disambiguationData":[OSD([subQ8])]})])],"derivedFrom":makeQuery(id+"F6.opExtrude","SWEPT_FACE",FACE,{"disambiguationData":[OSD([sQuery(id+"F5.wireOp",EDGE,"E188")])]})});}
            var sketch = newSketch(context, id + "F9", { "sketchPlane" : qUnion([Q0])});
            skLineSegment(sketch, "E218.bottom", {"start": v(-13.72, 49.42) * mm, "end": v(-12.7, 49.42) * mm});
            skLineSegment(sketch, "E218.top", {"start": v(-13.72, 47.62) * mm, "end": v(-12.7, 47.62) * mm});
            skLineSegment(sketch, "E218.left", {"start": v(-13.72, 49.42) * mm, "end": v(-13.72, 47.62) * mm});
            skLineSegment(sketch, "E218.right", {"start": v(-12.7, 49.42) * mm, "end": v(-12.7, 47.62) * mm});
            skLineSegment(sketch, "E219.bottom", {"start": v(-27.43, 49.42) * mm, "end": v(-26.42, 49.42) * mm});
            skLineSegment(sketch, "E219.top", {"start": v(-27.43, 47.62) * mm, "end": v(-26.42, 47.62) * mm});
            skLineSegment(sketch, "E219.left", {"start": v(-27.43, 49.42) * mm, "end": v(-27.43, 47.62) * mm});
            skLineSegment(sketch, "E219.right", {"start": v(-26.42, 49.42) * mm, "end": v(-26.42, 47.62) * mm});
            skLineSegment(sketch, "E220", {"start": v(-27.43, 47.62) * mm, "end": v(-26.92, 47.58) * mm});
            skLineSegment(sketch, "E221", {"start": v(-26.92, 47.58) * mm, "end": v(-26.42, 47.62) * mm});
            skLineSegment(sketch, "E222", {"start": v(-13.72, 47.62) * mm, "end": v(-13.2, 47.58) * mm});
            skPoint(sketch, "E222.endSnap0", {"position": v(-13.2, 47.62) * mm});
            skLineSegment(sketch, "E223", {"start": v(-13.2, 47.58) * mm, "end": v(-12.7, 47.62) * mm});
            skLineSegment(sketch, "E224.bottom", {"start": v(-41.15, 49.42) * mm, "end": v(-40.13, 49.42) * mm});
            skLineSegment(sketch, "E224.top", {"start": v(-41.15, 47.63) * mm, "end": v(-40.13, 47.63) * mm});
            skLineSegment(sketch, "E224.left", {"start": v(-41.15, 49.42) * mm, "end": v(-41.15, 47.63) * mm});
            skLineSegment(sketch, "E224.right", {"start": v(-40.13, 49.42) * mm, "end": v(-40.13, 47.63) * mm});
            skLineSegment(sketch, "E225", {"start": v(-41.15, 47.63) * mm, "end": v(-40.64, 47.58) * mm});
            skLineSegment(sketch, "E226", {"start": v(-40.64, 47.58) * mm, "end": v(-40.13, 47.63) * mm});
            skLineSegment(sketch, "E227.bottom", {"start": v(-68.58, 49.42) * mm, "end": v(-67.56, 49.42) * mm});
            skLineSegment(sketch, "E227.top", {"start": v(-68.58, 47.62) * mm, "end": v(-67.56, 47.62) * mm});
            skLineSegment(sketch, "E227.left", {"start": v(-68.58, 49.42) * mm, "end": v(-68.58, 47.62) * mm});
            skLineSegment(sketch, "E227.right", {"start": v(-67.56, 49.42) * mm, "end": v(-67.56, 47.62) * mm});
            skLineSegment(sketch, "E228", {"start": v(-68.58, 47.62) * mm, "end": v(-68.07, 47.58) * mm});
            skLineSegment(sketch, "E229", {"start": v(-68.07, 47.58) * mm, "end": v(-67.56, 47.62) * mm});
            skLineSegment(sketch, "E230.bottom", {"start": v(-82.3, 49.42) * mm, "end": v(-81.28, 49.42) * mm});
            skLineSegment(sketch, "E230.top", {"start": v(-82.3, 47.62) * mm, "end": v(-81.28, 47.62) * mm});
            skLineSegment(sketch, "E230.left", {"start": v(-82.3, 49.42) * mm, "end": v(-82.3, 47.62) * mm});
            skLineSegment(sketch, "E230.right", {"start": v(-81.28, 49.42) * mm, "end": v(-81.28, 47.62) * mm});
            skLineSegment(sketch, "E231", {"start": v(-82.3, 47.62) * mm, "end": v(-81.79, 47.58) * mm});
            skLineSegment(sketch, "E232", {"start": v(-81.79, 47.58) * mm, "end": v(-81.28, 47.62) * mm});
            skLineSegment(sketch, "E233.bottom", {"start": v(-96.01, 49.42) * mm, "end": v(-95, 49.42) * mm});
            skLineSegment(sketch, "E233.top", {"start": v(-96.01, 47.62) * mm, "end": v(-95, 47.62) * mm});
            skLineSegment(sketch, "E233.left", {"start": v(-96.01, 49.42) * mm, "end": v(-96.01, 47.62) * mm});
            skLineSegment(sketch, "E233.right", {"start": v(-95, 49.42) * mm, "end": v(-95, 47.62) * mm});
            skLineSegment(sketch, "E234", {"start": v(-96.01, 47.62) * mm, "end": v(-95.5, 47.58) * mm});
            skLineSegment(sketch, "E235", {"start": v(-95.5, 47.58) * mm, "end": v(-95, 47.62) * mm});
            skLineSegment(sketch, "E236.bottom", {"start": v(-109.73, 49.42) * mm, "end": v(-108.71, 49.42) * mm});
            skLineSegment(sketch, "E236.top", {"start": v(-109.73, 47.62) * mm, "end": v(-108.71, 47.62) * mm});
            skLineSegment(sketch, "E236.left", {"start": v(-109.73, 49.42) * mm, "end": v(-109.73, 47.62) * mm});
            skLineSegment(sketch, "E236.right", {"start": v(-108.71, 49.42) * mm, "end": v(-108.71, 47.62) * mm});
            skLineSegment(sketch, "E237", {"start": v(-109.73, 47.62) * mm, "end": v(-109.22, 47.58) * mm});
            skLineSegment(sketch, "E238", {"start": v(-109.22, 47.58) * mm, "end": v(-108.71, 47.62) * mm});
            skLineSegment(sketch, "E239.bottom", {"start": v(-54.86, 47.62) * mm, "end": v(-53.85, 47.62) * mm});
            skLineSegment(sketch, "E239.top", {"start": v(-54.86, 49.42) * mm, "end": v(-53.85, 49.42) * mm});
            skLineSegment(sketch, "E239.left", {"start": v(-54.86, 47.62) * mm, "end": v(-54.86, 49.42) * mm});
            skLineSegment(sketch, "E239.right", {"start": v(-53.85, 47.62) * mm, "end": v(-53.85, 49.42) * mm});
            skLineSegment(sketch, "E240", {"start": v(-54.86, 47.62) * mm, "end": v(-54.36, 47.58) * mm});
            skLineSegment(sketch, "E241", {"start": v(-54.36, 47.58) * mm, "end": v(-53.85, 47.62) * mm});
            skLineSegment(sketch, "E242.bottom", {"start": v(-123.44, 49.42) * mm, "end": v(-122.43, 49.42) * mm});
            skLineSegment(sketch, "E242.top", {"start": v(-123.44, 47.62) * mm, "end": v(-122.43, 47.62) * mm});
            skLineSegment(sketch, "E242.left", {"start": v(-123.44, 49.42) * mm, "end": v(-123.44, 47.62) * mm});
            skLineSegment(sketch, "E242.right", {"start": v(-122.43, 49.42) * mm, "end": v(-122.43, 47.62) * mm});
            skLineSegment(sketch, "E243", {"start": v(-123.44, 47.62) * mm, "end": v(-122.94, 47.58) * mm});
            skLineSegment(sketch, "E244", {"start": v(-122.94, 47.58) * mm, "end": v(-122.43, 47.62) * mm});
            skLineSegment(sketch, "E245.bottom", {"start": v(-137.16, 49.42) * mm, "end": v(-136.14, 49.42) * mm});
            skLineSegment(sketch, "E245.top", {"start": v(-137.16, 47.63) * mm, "end": v(-136.14, 47.63) * mm});
            skLineSegment(sketch, "E245.left", {"start": v(-137.16, 49.42) * mm, "end": v(-137.16, 47.63) * mm});
            skLineSegment(sketch, "E245.right", {"start": v(-136.14, 49.42) * mm, "end": v(-136.14, 47.63) * mm});
            skLineSegment(sketch, "E246", {"start": v(-137.16, 47.63) * mm, "end": v(-136.65, 47.58) * mm});
            skLineSegment(sketch, "E247", {"start": v(-136.65, 47.58) * mm, "end": v(-136.14, 47.63) * mm});
            skLineSegment(sketch, "E248.bottom", {"start": v(-150.88, 49.42) * mm, "end": v(-149.86, 49.42) * mm});
            skLineSegment(sketch, "E248.top", {"start": v(-150.88, 47.63) * mm, "end": v(-149.86, 47.63) * mm});
            skLineSegment(sketch, "E248.left", {"start": v(-150.88, 49.42) * mm, "end": v(-150.88, 47.63) * mm});
            skLineSegment(sketch, "E248.right", {"start": v(-149.86, 49.42) * mm, "end": v(-149.86, 47.63) * mm});
            skLineSegment(sketch, "E249", {"start": v(-150.88, 47.63) * mm, "end": v(-150.37, 47.58) * mm});
            skLineSegment(sketch, "E250", {"start": v(-150.37, 47.58) * mm, "end": v(-149.86, 47.63) * mm});
            skLineSegment(sketch, "E251.bottom", {"start": v(-163.58, 49.42) * mm, "end": v(-164.6, 49.42) * mm});
            skLineSegment(sketch, "E251.top", {"start": v(-163.58, 47.62) * mm, "end": v(-164.6, 47.62) * mm});
            skLineSegment(sketch, "E251.left", {"start": v(-163.58, 49.42) * mm, "end": v(-163.58, 47.62) * mm});
            skLineSegment(sketch, "E251.right", {"start": v(-164.6, 49.42) * mm, "end": v(-164.6, 47.62) * mm});
            skLineSegment(sketch, "E252", {"start": v(-164.6, 47.62) * mm, "end": v(-164.08, 47.58) * mm});
            skLineSegment(sketch, "E253", {"start": v(-164.08, 47.58) * mm, "end": v(-163.58, 47.62) * mm});
            skLineSegment(sketch, "E254.bottom", {"start": v(-178.3, 49.42) * mm, "end": v(-177.3, 49.42) * mm});
            skLineSegment(sketch, "E254.top", {"start": v(-178.3, 47.63) * mm, "end": v(-177.3, 47.63) * mm});
            skLineSegment(sketch, "E254.left", {"start": v(-178.3, 49.42) * mm, "end": v(-178.3, 47.63) * mm});
            skLineSegment(sketch, "E254.right", {"start": v(-177.3, 49.42) * mm, "end": v(-177.3, 47.63) * mm});
            skLineSegment(sketch, "E255", {"start": v(-178.3, 47.63) * mm, "end": v(-177.8, 47.58) * mm});
            skLineSegment(sketch, "E256", {"start": v(-177.8, 47.58) * mm, "end": v(-177.3, 47.63) * mm});
            skSolve(sketch);
        }
        {
            var Q0;
            Q0 = qSketchRegion(id + "F9", true);
            extrude(context, id + "F10", {"entities" : qUnion([Q0]), "operationType" : NewBodyOperationType.REMOVE, "oppositeDirection" : true, "depth" : 25.4 * mm});
        }
        {
            var Q0;
            Q0=makeQuery(id+"F1.opExtrude","SWEPT_FACE",FACE,{"disambiguationData":[OSD([sQuery(id+"F0.wireOp",EDGE,"E9")])]});
            var sketch = newSketch(context, id + "F11", { "sketchPlane" : qUnion([Q0])});
            skLineSegment(sketch, "E257.right", {"start": v(-39.5, 0) * mm, "end": v(-39.5, 3.18) * mm});
            skLineSegment(sketch, "E258", {"start": v(-18.35, 0) * mm, "end": v(-18.35, 20.93) * mm});
            skLineSegment(sketch, "E259.bottom", {"start": v(-19.87, 25.1) * mm, "end": v(-16.84, 25.1) * mm});
            skLineSegment(sketch, "E259.top", {"start": v(-19.87, -1.5) * mm, "end": v(-16.84, -1.5) * mm});
            skLineSegment(sketch, "E259.left", {"start": v(-19.87, 25.1) * mm, "end": v(-19.87, -1.5) * mm});
            skLineSegment(sketch, "E259.right", {"start": v(-16.84, 25.1) * mm, "end": v(-16.84, -1.5) * mm});
            skSolve(sketch);
        }
        {
            var Q0;
            Q0 = qSketchRegion(id + "F11", true);
            extrude(context, id + "F12", {"entities" : qUnion([Q0]), "depth" : 25.4 * mm});
        }
        {
            var Q0;
            Q0=makeQuery(id+"F1.opExtrude","SWEPT_BODY",BODY,{"disambiguationData":[OSD([sQuery(id+"F0.wireOp",EDGE,"E0"),sQuery(id+"F0.wireOp",EDGE,"E1"),sQuery(id+"F0.wireOp",EDGE,"E2"),sQuery(id+"F0.wireOp",EDGE,"E3"),sQuery(id+"F0.wireOp",EDGE,"E4"),sQuery(id+"F0.wireOp",EDGE,"E5"),sQuery(id+"F0.wireOp",EDGE,"E6"),sQuery(id+"F0.wireOp",EDGE,"E7"),sQuery(id+"F0.wireOp",EDGE,"E8"),sQuery(id+"F0.wireOp",EDGE,"E9"),sQuery(id+"F0.wireOp",EDGE,"E10"),sQuery(id+"F0.wireOp",EDGE,"E12.MirrorCS"),sQuery(id+"F0.wireOp",EDGE,"E13.MirrorCS"),sQuery(id+"F0.wireOp",EDGE,"E14.MirrorCS"),sQuery(id+"F0.wireOp",EDGE,"E15.MirrorCS"),sQuery(id+"F0.wireOp",EDGE,"E16.MirrorCS"),sQuery(id+"F0.wireOp",EDGE,"E17.MirrorCS"),sQuery(id+"F0.wireOp",EDGE,"E18.MirrorCS"),sQuery(id+"F0.wireOp",EDGE,"E19.MirrorCS"),sQuery(id+"F0.wireOp",EDGE,"E20.MirrorCS"),sQuery(id+"F0.wireOp",EDGE,"E22.MirrorCS"),sQuery(id+"F0.wireOp",EDGE,"E23.MirrorCS"),sQuery(id+"F0.wireOp",EDGE,"E24.MirrorCS"),sQuery(id+"F0.wireOp",EDGE,"E25.MirrorCS"),sQuery(id+"F0.wireOp",EDGE,"E26.MirrorCS"),sQuery(id+"F0.wireOp",EDGE,"E27.MirrorCS"),sQuery(id+"F0.wireOp",EDGE,"E28.MirrorCS"),sQuery(id+"F0.wireOp",EDGE,"E29.MirrorCS"),sQuery(id+"F0.wireOp",EDGE,"E30.MirrorCS"),sQuery(id+"F0.wireOp",EDGE,"E32.MirrorCS"),sQuery(id+"F0.wireOp",EDGE,"E33.MirrorCS"),sQuery(id+"F0.wireOp",EDGE,"E35.MirrorCS"),sQuery(id+"F0.wireOp",EDGE,"E36.MirrorCS"),sQuery(id+"F0.wireOp",EDGE,"E37.MirrorCS"),sQuery(id+"F0.wireOp",EDGE,"E38.MirrorCS"),sQuery(id+"F0.wireOp",EDGE,"E39.MirrorCS"),sQuery(id+"F0.wireOp",EDGE,"E41.MirrorCS"),sQuery(id+"F0.wireOp",EDGE,"E34.MirrorCS"),sQuery(id+"F0.wireOp",EDGE,"E42.MirrorCS"),sQuery(id+"F0.wireOp",EDGE,"E40.MirrorCS"),sQuery(id+"F0.wireOp",EDGE,"E43.MirrorCS"),sQuery(id+"F0.wireOp",EDGE,"E44.MirrorCS"),sQuery(id+"F0.wireOp",EDGE,"E45.MirrorCS"),sQuery(id+"F0.wireOp",EDGE,"E46.MirrorCS"),sQuery(id+"F0.wireOp",EDGE,"E47.MirrorCS"),sQuery(id+"F0.wireOp",EDGE,"E49.MirrorCS"),sQuery(id+"F0.wireOp",EDGE,"E48.MirrorCS"),sQuery(id+"F0.wireOp",EDGE,"E50.MirrorCS"),sQuery(id+"F0.wireOp",EDGE,"E51.MirrorCS"),sQuery(id+"F0.wireOp",EDGE,"E52.MirrorCS"),sQuery(id+"F0.wireOp",EDGE,"E53.MirrorCS"),sQuery(id+"F0.wireOp",EDGE,"E54.MirrorCS"),sQuery(id+"F0.wireOp",EDGE,"E55.MirrorCS"),sQuery(id+"F0.wireOp",EDGE,"E56.MirrorCS"),sQuery(id+"F0.wireOp",EDGE,"E57.MirrorCS"),sQuery(id+"F0.wireOp",EDGE,"E58.MirrorCS"),sQuery(id+"F0.wireOp",EDGE,"E61.MirrorCS"),sQuery(id+"F0.wireOp",EDGE,"E62.MirrorCS"),sQuery(id+"F0.wireOp",EDGE,"E60.MirrorCS"),sQuery(id+"F0.wireOp",EDGE,"E63.MirrorCS"),sQuery(id+"F0.wireOp",EDGE,"E64.MirrorCS"),sQuery(id+"F0.wireOp",EDGE,"E65.MirrorCS"),sQuery(id+"F0.wireOp",EDGE,"E67.MirrorCS"),sQuery(id+"F0.wireOp",EDGE,"E68.MirrorCS"),sQuery(id+"F0.wireOp",EDGE,"E66.MirrorCS"),sQuery(id+"F0.wireOp",EDGE,"E69.MirrorCS"),sQuery(id+"F0.wireOp",EDGE,"E70.MirrorCS"),sQuery(id+"F0.wireOp",EDGE,"E71.MirrorCS"),sQuery(id+"F0.wireOp",EDGE,"E72.MirrorCS"),sQuery(id+"F0.wireOp",EDGE,"E73.MirrorCS"),sQuery(id+"F0.wireOp",EDGE,"E74.MirrorCS"),sQuery(id+"F0.wireOp",EDGE,"E75.MirrorCS"),sQuery(id+"F0.wireOp",EDGE,"E76.MirrorCS"),sQuery(id+"F0.wireOp",EDGE,"E77.MirrorCS"),sQuery(id+"F0.wireOp",EDGE,"E78.MirrorCS"),sQuery(id+"F0.wireOp",EDGE,"E79.MirrorCS"),sQuery(id+"F0.wireOp",EDGE,"E80.MirrorCS"),sQuery(id+"F0.wireOp",EDGE,"E81.MirrorCS"),sQuery(id+"F0.wireOp",EDGE,"E82.MirrorCS"),sQuery(id+"F0.wireOp",EDGE,"E83.MirrorCS"),sQuery(id+"F0.wireOp",EDGE,"E84.MirrorCS"),sQuery(id+"F0.wireOp",EDGE,"E85.MirrorCS"),sQuery(id+"F0.wireOp",EDGE,"E86.MirrorCS"),sQuery(id+"F0.wireOp",EDGE,"E87.MirrorCS"),sQuery(id+"F0.wireOp",EDGE,"E88.MirrorCS"),sQuery(id+"F0.wireOp",EDGE,"E89.MirrorCS"),sQuery(id+"F0.wireOp",EDGE,"E91.MirrorCS"),sQuery(id+"F0.wireOp",EDGE,"E92.MirrorCS"),sQuery(id+"F0.wireOp",EDGE,"E93.MirrorCS"),sQuery(id+"F0.wireOp",EDGE,"E96.MirrorCS"),sQuery(id+"F0.wireOp",EDGE,"E97.MirrorCS"),sQuery(id+"F0.wireOp",EDGE,"E98.MirrorCS"),sQuery(id+"F0.wireOp",EDGE,"E99.MirrorCS"),sQuery(id+"F0.wireOp",EDGE,"E100.MirrorCS"),sQuery(id+"F0.wireOp",EDGE,"E101.MirrorCS"),sQuery(id+"F0.wireOp",EDGE,"E102.MirrorCS"),sQuery(id+"F0.wireOp",EDGE,"E90.MirrorCS"),sQuery(id+"F0.wireOp",EDGE,"E103.MirrorCS"),sQuery(id+"F0.wireOp",EDGE,"E94.MirrorCS"),sQuery(id+"F0.wireOp",EDGE,"E104.MirrorCS"),sQuery(id+"F0.wireOp",EDGE,"E105.MirrorCS"),sQuery(id+"F0.wireOp",EDGE,"E106.MirrorCS"),sQuery(id+"F0.wireOp",EDGE,"E107.MirrorCS"),sQuery(id+"F0.wireOp",EDGE,"E109.MirrorCS"),sQuery(id+"F0.wireOp",EDGE,"E110.MirrorCS"),sQuery(id+"F0.wireOp",EDGE,"E112.MirrorCS"),sQuery(id+"F0.wireOp",EDGE,"E113.MirrorCS"),sQuery(id+"F0.wireOp",EDGE,"E114.MirrorCS"),sQuery(id+"F0.wireOp",EDGE,"E116.MirrorCS"),sQuery(id+"F0.wireOp",EDGE,"E117.MirrorCS"),sQuery(id+"F0.wireOp",EDGE,"E118.MirrorCS"),sQuery(id+"F0.wireOp",EDGE,"E119.MirrorCS"),sQuery(id+"F0.wireOp",EDGE,"E120.MirrorCS"),sQuery(id+"F0.wireOp",EDGE,"E121.MirrorCS"),sQuery(id+"F0.wireOp",EDGE,"E122.MirrorCS"),sQuery(id+"F0.wireOp",EDGE,"E124.MirrorCS"),sQuery(id+"F0.wireOp",EDGE,"E125.MirrorCS"),sQuery(id+"F0.wireOp",EDGE,"E126.MirrorCS"),sQuery(id+"F0.wireOp",EDGE,"E127.MirrorCS"),sQuery(id+"F0.wireOp",EDGE,"E128.MirrorCS"),sQuery(id+"F0.wireOp",EDGE,"E129.MirrorCS"),sQuery(id+"F0.wireOp",EDGE,"E130.MirrorCS"),sQuery(id+"F0.wireOp",EDGE,"E131.MirrorCS"),sQuery(id+"F0.wireOp",EDGE,"E132.MirrorCS"),sQuery(id+"F0.wireOp",EDGE,"E133.MirrorCS"),sQuery(id+"F0.wireOp",EDGE,"E134"),sQuery(id+"F0.wireOp",EDGE,"E135.MirrorCS"),sQuery(id+"F0.wireOp",EDGE,"E136"),sQuery(id+"F0.wireOp",EDGE,"E137"),sQuery(id+"F0.wireOp",EDGE,"E138"),sQuery(id+"F0.wireOp",EDGE,"E139"),sQuery(id+"F0.wireOp",EDGE,"E140"),sQuery(id+"F0.wireOp",EDGE,"E141"),sQuery(id+"F0.wireOp",EDGE,"E142"),sQuery(id+"F0.wireOp",EDGE,"E143"),sQuery(id+"F0.wireOp",EDGE,"E144"),sQuery(id+"F0.wireOp",EDGE,"E145"),sQuery(id+"F0.wireOp",EDGE,"E146"),sQuery(id+"F0.wireOp",EDGE,"E147"),sQuery(id+"F0.wireOp",EDGE,"E148"),sQuery(id+"F0.wireOp",EDGE,"E149"),sQuery(id+"F0.wireOp",EDGE,"E150"),sQuery(id+"F0.wireOp",EDGE,"E151"),sQuery(id+"F0.wireOp",EDGE,"E152"),sQuery(id+"F0.wireOp",EDGE,"E153"),sQuery(id+"F0.wireOp",EDGE,"E154"),sQuery(id+"F0.wireOp",EDGE,"E155"),sQuery(id+"F0.wireOp",EDGE,"E156"),sQuery(id+"F0.wireOp",EDGE,"E157"),sQuery(id+"F0.wireOp",EDGE,"E158"),sQuery(id+"F0.wireOp",EDGE,"E159"),sQuery(id+"F0.wireOp",EDGE,"E160"),sQuery(id+"F0.wireOp",EDGE,"E161"),sQuery(id+"F0.wireOp",EDGE,"E162"),sQuery(id+"F0.wireOp",EDGE,"E163"),sQuery(id+"F0.wireOp",EDGE,"E164"),sQuery(id+"F0.wireOp",EDGE,"E165"),sQuery(id+"F0.wireOp",EDGE,"E166"),sQuery(id+"F0.wireOp",EDGE,"E167"),sQuery(id+"F0.wireOp",EDGE,"E168"),sQuery(id+"F0.wireOp",EDGE,"E169"),sQuery(id+"F0.wireOp",EDGE,"E170"),sQuery(id+"F0.wireOp",EDGE,"E171"),sQuery(id+"F0.wireOp",EDGE,"E172"),sQuery(id+"F0.wireOp",EDGE,"E173"),sQuery(id+"F0.wireOp",EDGE,"E174"),sQuery(id+"F0.wireOp",EDGE,"E175"),sQuery(id+"F0.wireOp",EDGE,"E176")])]});
            var Q1;
            Q1=makeQuery(id+"F12.opExtrude","SWEPT_FACE",FACE,{"disambiguationData":[OSD([sQuery(id+"F11.wireOp",EDGE,"E259.left")])]});
            mirror(context, id + "F13", {"entities" : qUnion([Q0]), "mirrorPlane" : qUnion([Q1])});
        }
        {
            var Q0;
            Q0=makeQuery(id+"F1.opExtrude","SWEPT_FACE",FACE,{"disambiguationData":[OSD([sQuery(id+"F0.wireOp",EDGE,"E9")])]});
            var sketch = newSketch(context, id + "F14", { "sketchPlane" : qUnion([Q0])});
            skLineSegment(sketch, "E260.bottom", {"start": v(0, 0) * mm, "end": v(-39.73, 0) * mm});
            skLineSegment(sketch, "E260.top", {"start": v(0, 3.18) * mm, "end": v(-39.73, 3.18) * mm});
            skLineSegment(sketch, "E260.left", {"start": v(0, 0) * mm, "end": v(0, 3.18) * mm});
            skLineSegment(sketch, "E260.right", {"start": v(-39.73, 0) * mm, "end": v(-39.73, 3.17) * mm});
            skSolve(sketch);
        }
        {
            var Q0;
            Q0 = qSketchRegion(id + "F14", true);
            extrude(context, id + "F15", {"entities" : qUnion([Q0]), "oppositeDirection" : true, "depth" : 191 * mm});
        }
        {
            var Q0;
            Q0 = qSketchRegion(id + "F14", true);
            extrude(context, id + "F16", {"entities" : qUnion([Q0]), "operationType" : NewBodyOperationType.ADD, "oppositeDirection" : true, "depth" : 191 * mm});
        }
    });
